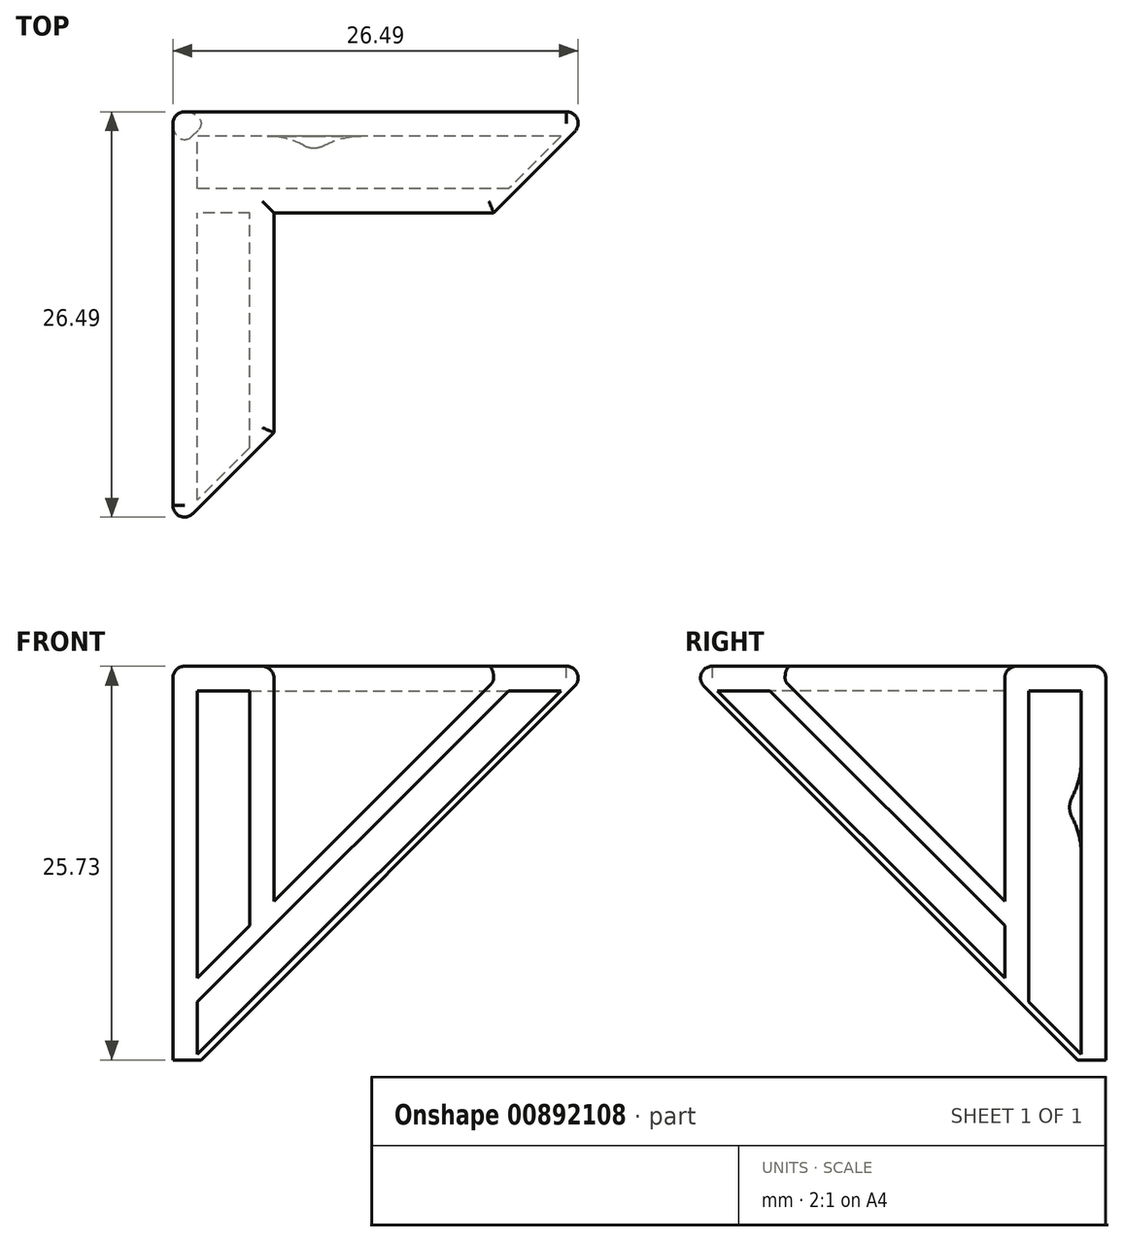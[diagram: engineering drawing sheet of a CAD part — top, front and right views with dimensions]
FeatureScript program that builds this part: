
annotation { "Feature Type Name" : "Feature", "Feature Type Description" : "" }
export const myFeature = defineFeature(function(context is Context, id is Id, definition is map)
    precondition{}
    {
        {
            var Q0;
            Q0=qCreatedBy(makeId("Top.planeOp"),FACE);
            var sketch = newSketch(context, id + "F0", { "sketchPlane" : qUnion([Q0])});
            skLineSegment(sketch, "E0", {"start": v(0, 0) * mm, "end": v(21.97, 0) * mm});
            skLineSegment(sketch, "E1", {"start": v(21.97, 0) * mm, "end": v(21.97, 6.6) * mm});
            skLineSegment(sketch, "E2", {"start": v(21.97, 6.6) * mm, "end": v(-6.6, 6.6) * mm});
            skLineSegment(sketch, "E3", {"start": v(-6.6, 6.6) * mm, "end": v(-6.6, -21.97) * mm});
            skLineSegment(sketch, "E4", {"start": v(-6.6, -21.97) * mm, "end": v(0, -21.97) * mm});
            skLineSegment(sketch, "E5", {"start": v(0, -21.97) * mm, "end": v(0, 0) * mm});
            skSolve(sketch);
        }
        {
            var Q0;
            Q0 = qSketchRegion(id + "F0", true);
            extrude(context, id + "F1", {"entities" : qUnion([Q0]), "oppositeDirection" : true, "depth" : 28.57 * mm, "offsetDistance" : 25.4 * mm});
        }
        {
            var Q0;
            Q0=makeQuery(id+"F1.opExtrude","CAP_VERTEX",VERTEX,{"disambiguationData":[OSD([sQuery(id+"F0.wireOp",EDGE,"E2"),sQuery(id+"F0.wireOp",EDGE,"E3")])],"isStart":false});
            var Q1;
            Q1=makeQuery(id+"F1.opExtrude","CAP_VERTEX",VERTEX,{"disambiguationData":[OSD([sQuery(id+"F0.wireOp",EDGE,"E3"),sQuery(id+"F0.wireOp",EDGE,"E4")])],"isStart":true});
            var Q2;
            Q2=makeQuery(id+"F1.opExtrude","CAP_VERTEX",VERTEX,{"disambiguationData":[OSD([sQuery(id+"F0.wireOp",EDGE,"E1"),sQuery(id+"F0.wireOp",EDGE,"E2")])],"isStart":true});
            cPlane(context, id + "F2", {"entities" : qUnion([Q0, Q1, Q2]), "cplaneType" : CPlaneType.THREE_POINT, "offset" : 25.4 * mm, "width" : 152.4 * mm, "height" : 152.4 * mm});
        }
        {
            var Q0;
            Q0=qCreatedBy(id+"F2.planeOp",FACE);
            var sketch = newSketch(context, id + "F3", { "sketchPlane" : qUnion([Q0])});
            skCircle(sketch, "E6", {"center": v(0, 0) * mm, "radius": 38.1 * mm});
            skSolve(sketch);
        }
        {
            var Q0;
            Q0=makeQuery(id+"F3.imprint","IMPRINT",FACE,{"disambiguationData":[TD([[makeQuery(id+"F3.imprint","IMPRINT",EDGE,{"derivedFrom":sQuery(id+"F3.wireOp",EDGE,"E6")}),1.0]])]});
            extrude(context, id + "F4", {"entities" : qUnion([Q0]), "operationType" : NewBodyOperationType.REMOVE, "endBound" : BoundingType.THROUGH_ALL, "depth" : 25.4 * mm, "offsetDistance" : 25.4 * mm});
        }
        {
            var Q0;
            Q0=makeQuery(id+"F1.opExtrude","CAP_FACE",FACE,{"disambiguationData":[OSD([sQuery(id+"F0.wireOp",EDGE,"E0"),sQuery(id+"F0.wireOp",EDGE,"E1"),sQuery(id+"F0.wireOp",EDGE,"E2"),sQuery(id+"F0.wireOp",EDGE,"E3"),sQuery(id+"F0.wireOp",EDGE,"E4"),sQuery(id+"F0.wireOp",EDGE,"E5")])],"isStart":true});
            cPlane(context, id + "F5", {"entities" : qUnion([Q0]), "cplaneType" : CPlaneType.OFFSET, "offset" : 1.6 * mm, "oppositeDirection" : true, "width" : 152.4 * mm, "height" : 152.4 * mm});
        }
        {
            var Q0;
            Q0=qCreatedBy(id+"F5.planeOp",FACE);
            var sketch = newSketch(context, id + "F6", { "sketchPlane" : qUnion([Q0])});
            skLineSegment(sketch, "E7.bottom", {"start": v(-5, 5) * mm, "end": v(21.97, 5) * mm});
            skLineSegment(sketch, "E7.top", {"start": v(-5, 1.57) * mm, "end": v(21.97, 1.57) * mm});
            skLineSegment(sketch, "E7.left", {"start": v(-5, 5) * mm, "end": v(-5, 1.57) * mm});
            skLineSegment(sketch, "E7.right", {"start": v(21.97, 5) * mm, "end": v(21.97, 1.57) * mm});
            skLineSegment(sketch, "E8.bottom", {"start": v(-5, 0) * mm, "end": v(-1.57, 0) * mm});
            skLineSegment(sketch, "E8.top", {"start": v(-5, -21.97) * mm, "end": v(-1.57, -21.97) * mm});
            skLineSegment(sketch, "E8.left", {"start": v(-5, 0) * mm, "end": v(-5, -21.97) * mm});
            skLineSegment(sketch, "E8.right", {"start": v(-1.57, 0) * mm, "end": v(-1.57, -21.97) * mm});
            skSolve(sketch);
        }
        {
            var Q0;
            Q0 = qSketchRegion(id + "F6", true);
            extrude(context, id + "F7", {"entities" : qUnion([Q0]), "operationType" : NewBodyOperationType.REMOVE, "endBound" : BoundingType.THROUGH_ALL, "oppositeDirection" : true, "depth" : 25.4 * mm, "offsetDistance" : 25.4 * mm});
        }
        {
            var Q0;
            Q0=makeQuery(id+"F7.boolean.opBoolean","COPY",FACE,{"derivedFrom":makeQuery(id+"F7.opExtrude","SWEPT_FACE",FACE,{"disambiguationData":[OSD([sQuery(id+"F6.wireOp",EDGE,"E7.left")])]})});
            cPlane(context, id + "F8", {"entities" : qUnion([Q0]), "cplaneType" : CPlaneType.OFFSET, "offset" : 7.62 * mm, "width" : 152.4 * mm, "height" : 152.4 * mm});
        }
        {
            var Q0;
            Q0=qCreatedBy(id+"F8.planeOp",FACE);
            var sketch = newSketch(context, id + "F9", { "sketchPlane" : qUnion([Q0])});
            skLineSegment(sketch, "E9.0.1", {"start": v(5, -1.6) * mm, "end": v(5, -25.37) * mm, "construction": true});
            skLineSegment(sketch, "E9.0.2", {"start": v(5, -25.37) * mm, "end": v(5, -1.6) * mm, "construction": true});
            skLineSegment(sketch, "E10", {"start": v(5, -10.5) * mm, "end": v(5, -9.22) * mm});
            skLineSegment(sketch, "E11", {"start": v(5, -9.22) * mm, "end": v(4.24, -9.22) * mm});
            skLineSegment(sketch, "E12", {"start": v(4.24, -9.74) * mm, "end": v(4.24, -9.22) * mm, "construction": true});
            skArc(sketch, "E13", {"start": v(4.24, -9.22) * mm, "mid": v(4.45, -9.96) * mm, "end": v(5, -10.5) * mm});
            skSolve(sketch);
        }
        {
            var Q0;
            Q0 = qSketchRegion(id + "F9", true);
            var Q1;
            Q1=sQuery(id+"F9.wireOp",EDGE,"E11");
            revolve(context, id + "F10", {"operationType" : NewBodyOperationType.ADD, "surfaceOperationType" : NewSurfaceOperationType.NEW, "entities" : qUnion([Q0]), "axis" : qUnion([Q1]), "revolveType" : RevolveType.FULL});
        }
        {
            var Q0;
            Q0=makeQuery(id+"F1.opExtrude","CAP_FACE",FACE,{"disambiguationData":[OSD([sQuery(id+"F0.wireOp",EDGE,"E0"),sQuery(id+"F0.wireOp",EDGE,"E1"),sQuery(id+"F0.wireOp",EDGE,"E2"),sQuery(id+"F0.wireOp",EDGE,"E3"),sQuery(id+"F0.wireOp",EDGE,"E4"),sQuery(id+"F0.wireOp",EDGE,"E5")])],"isStart":true});
            var sketch = newSketch(context, id + "F11", { "sketchPlane" : qUnion([Q0])});
            skLineSegment(sketch, "E14", {"start": v(-6.6, 6.6) * mm, "end": v(0, 0) * mm, "construction": true});
            skSolve(sketch);
        }
        {
            var Q0;
            Q0=sQuery(id+"F11.wireOp",EDGE,"E14");
            var Q1;
            {var subQ3=sQuery(id+"F0.wireOp",EDGE,"E2");Q1=makeQuery(id+"F11.imprint","IMPRINT",FACE,{"disambiguationData":[TD([[makeQuery(id+"F11.imprint","IMPRINT",EDGE,{"derivedFrom":makeQuery(id+"F1.opExtrude","CAP_EDGE",EDGE,{"disambiguationData":[OSD([subQ3])],"isStart":true})}),1.0]])]});}
            cPlane(context, id + "F12", {"entities" : qUnion([Q0, Q1]), "cplaneType" : CPlaneType.LINE_ANGLE, "offset" : 25.4 * mm, "angle" : 90 * degree, "width" : 152.4 * mm, "height" : 152.4 * mm});
        }
        {
            var Q0;
            Q0=makeQuery(id+"F10.opRevolve","SWEPT_FACE",FACE,{"disambiguationData":[OSD([sQuery(id+"F9.wireOp",EDGE,"E13")])]});
            var Q1;
            Q1=makeQuery(id+"FdODtfPfk0w7T5c_1.1.F10.opRevolve","SWEPT_FACE",FACE,{"disambiguationData":[OSD([sQuery(id+"F9.wireOp",EDGE,"E13")])]});
            fillet(context, id + "F13", {"entities" : qUnion([Q0, Q1]), "radius" : 5.08 * mm, "tangentPropagation" : true, "allowEdgeOverflow" : false});
        }
        {
            var Q0;
            Q0=makeQuery(id+"F1.opExtrude","SWEPT_FACE",FACE,{"disambiguationData":[OSD([sQuery(id+"F0.wireOp",EDGE,"E2")])]});
            var Q1;
            Q1=makeQuery(id+"F1.opExtrude","SWEPT_FACE",FACE,{"disambiguationData":[OSD([sQuery(id+"F0.wireOp",EDGE,"E3")])]});
            var Q2;
            Q2=makeQuery(id+"F1.opExtrude","CAP_FACE",FACE,{"disambiguationData":[OSD([sQuery(id+"F0.wireOp",EDGE,"E0"),sQuery(id+"F0.wireOp",EDGE,"E1"),sQuery(id+"F0.wireOp",EDGE,"E2"),sQuery(id+"F0.wireOp",EDGE,"E3"),sQuery(id+"F0.wireOp",EDGE,"E4"),sQuery(id+"F0.wireOp",EDGE,"E5")])],"isStart":true});
            fillet(context, id + "F14", {"entities" : qUnion([Q0, Q1, Q2]), "radius" : 0.76 * mm, "tangentPropagation" : true, "allowEdgeOverflow" : false});
        }
        {
            var Q0;
            Q0=makeQuery(id+"F1.opExtrude","SWEPT_FACE",FACE,{"disambiguationData":[OSD([sQuery(id+"F0.wireOp",EDGE,"E3")])]});
            var sketch = newSketch(context, id + "F15", { "sketchPlane" : qUnion([Q0])});
            skPoint(sketch, "E15.0", {"position": v(-6.6, -0.76) * mm});
            skLineSegment(sketch, "E16.0", {"start": v(-6.6, -25.73) * mm, "end": v(-6.6, -0.76) * mm, "construction": true});
            skLineSegment(sketch, "E17", {"start": v(19.67, -1.3) * mm, "end": v(-5.3, -26.27) * mm, "construction": true});
            skLineSegment(sketch, "E18.bottom", {"start": v(-6.6, -25.73) * mm, "end": v(-4.76, -25.73) * mm});
            skLineSegment(sketch, "E18.top", {"start": v(-6.6, -28.75) * mm, "end": v(-4.76, -28.75) * mm});
            skLineSegment(sketch, "E18.left", {"start": v(-6.6, -25.73) * mm, "end": v(-6.6, -28.75) * mm});
            skLineSegment(sketch, "E18.right", {"start": v(-4.76, -25.73) * mm, "end": v(-4.76, -28.75) * mm});
            skSolve(sketch);
        }
        {
            var Q0;
            Q0 = qSketchRegion(id + "F15", true);
            extrude(context, id + "F16", {"entities" : qUnion([Q0]), "operationType" : NewBodyOperationType.REMOVE, "endBound" : BoundingType.THROUGH_ALL, "oppositeDirection" : true, "depth" : 25.4 * mm, "offsetDistance" : 25.4 * mm});
        }
    });
